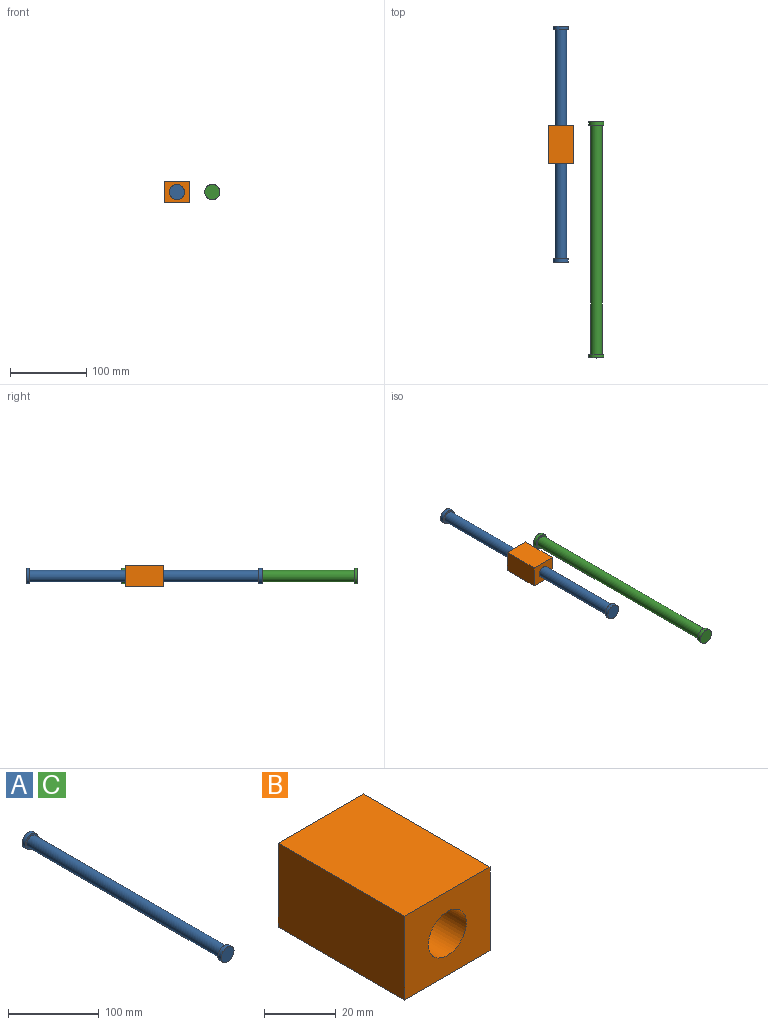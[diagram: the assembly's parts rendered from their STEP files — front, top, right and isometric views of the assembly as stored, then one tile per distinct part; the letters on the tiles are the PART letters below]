
ASSEMBLY  parts=3 mates=1
PART A: 7 faces, bbox 20x310x20 mm
  f0: cylinder r=7.5mm len=300mm, axis (0,1,0), area 14137.2mm2, adj f3,f6
  f1: cylinder r=10mm len=20mm, axis (0,1,0), area 314.2mm2, adj f2,f3
  f2: plane 20x20mm, normal (0,-1,0), area 314.2mm2, adj f1
  f3: plane 20x20mm, normal (0,1,0), area 137.4mm2, adj f0,f1
  f4: cylinder r=10mm len=20mm, axis (0,-1,0), area 314.2mm2, adj f5,f6
  f5: plane 20x20mm, normal (0,1,0), area 314.2mm2, adj f4
  f6: plane 20x20mm, normal (0,-1,0), area 137.4mm2, adj f0,f4
PART B: 7 faces, bbox 33.7x50x28.7 mm
  f0: plane 50x28.69mm, normal (1,0,0), area 1434.3mm2, adj f1,f3,f5,f6
  f1: plane 50x33.75mm, normal (0,0,1), area 1687.4mm2, adj f0,f2,f5,f6
  f2: plane 50x28.69mm, normal (-1,0,0), area 1434.3mm2, adj f1,f3,f5,f6
  f3: plane 50x33.75mm, normal (0,0,-1), area 1687.4mm2, adj f0,f2,f5,f6
  f4: cylinder r=7.5mm len=50mm, axis (0,1,0), area 2356.2mm2, adj f5,f6
  f5: plane 33.75x28.69mm, normal (0,-1,0), area 791.4mm2, adj f0,f1,f2,f3,f4
  f6: plane 33.75x28.69mm, normal (0,1,0), area 791.4mm2, adj f0,f1,f2,f3,f4
PART C: same geometry as A
PLACE A t=(-8.2,108.06,-56.29)mm
PLACE B t=(38.34,-17.26,-56.29)mm fixed
PLACE C t=(38.34,-17.26,-56.29)mm
MATE slider A.f0 <-> B.f4  axis (0,1,0) through (-8.2,-41.94,-56.29)mm
